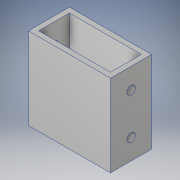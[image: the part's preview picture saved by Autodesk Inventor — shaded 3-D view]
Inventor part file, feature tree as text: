
AUTODESK INVENTOR PART (.ipt)
format: ipt  version: 2018 (Build 220112000, 112)  size: 123,392 bytes
history: native  units: in
note: dims shown in document units (in); Inventor stores cm internally (conversion verified against a paired STEP export)
features: extrude x2, sketch x2
ambient origin geometry x8: Origin, YZ Plane, XZ Plane, XY Plane, X Axis, Y Axis, Z Axis, Center Point
bodies: Solid1 (feature_tree)
feature tree (4):
  extrude  "Extrusion1"  Depth=1.0in
  extrude  "Extrusion2"  Depth=0.125in
  sketch  "Sketch1"  dims[d0=2.0in d1=1.0in]
  sketch  "Sketch2"  dims[d2=0.125in d3=0.125in d4=0.125in d5=0.125in d6=2.0in d7=0.0in d8=0.5in d9=1.0in d10=0.2in d11=2.4375in d12=0.0in]
